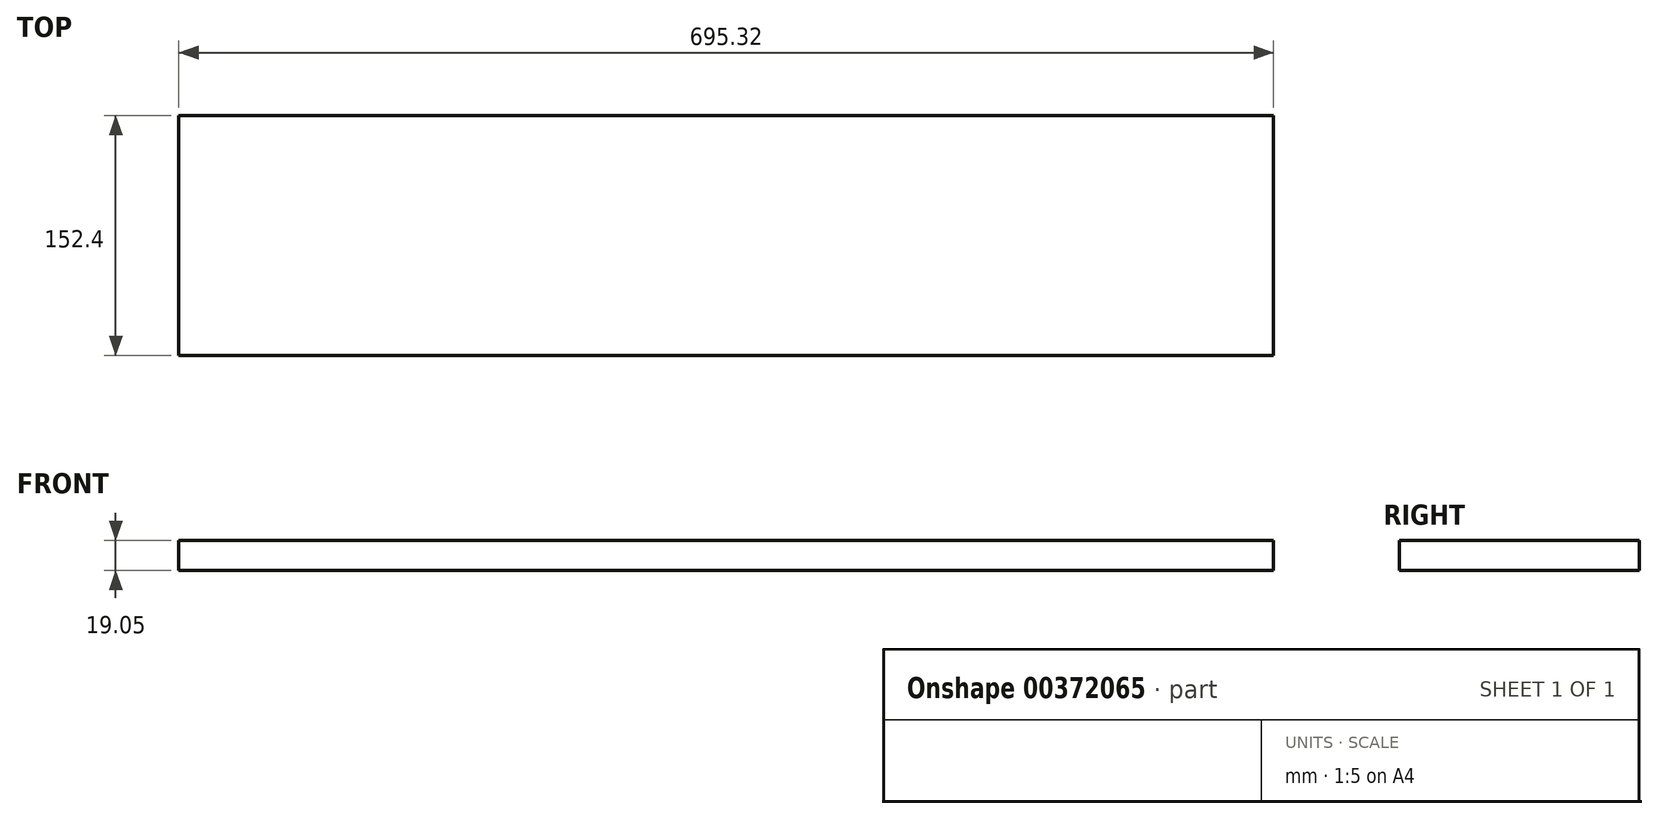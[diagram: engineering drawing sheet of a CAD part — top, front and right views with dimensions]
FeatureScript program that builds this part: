
annotation { "Feature Type Name" : "Feature", "Feature Type Description" : "" }
export const myFeature = defineFeature(function(context is Context, id is Id, definition is map)
    precondition{}
    {
        {
            var Q0;
            Q0=qCreatedBy(makeId("Top.planeOp"),FACE);
            var sketch = newSketch(context, id + "F0", { "sketchPlane" : qUnion([Q0])});
            skLineSegment(sketch, "E0.bottom", {"start": v(0, 0) * mm, "end": v(695.33, 0) * mm});
            skLineSegment(sketch, "E0.top", {"start": v(0, 152.4) * mm, "end": v(695.33, 152.4) * mm});
            skLineSegment(sketch, "E0.left", {"start": v(0, 0) * mm, "end": v(0, 152.4) * mm});
            skLineSegment(sketch, "E0.right", {"start": v(695.33, 0) * mm, "end": v(695.33, 152.4) * mm});
            skSolve(sketch);
        }
        {
            var Q0;
            Q0=makeQuery(id+"F0.imprint","IMPRINT",FACE,{"disambiguationData":[TD([[makeQuery(id+"F0.imprint","IMPRINT",EDGE,{"derivedFrom":sQuery(id+"F0.wireOp",EDGE,"E0.bottom")}),1.0]])]});
            extrude(context, id + "F1", {"entities" : qUnion([Q0]), "oppositeDirection" : true, "depth" : 19.05 * mm});
        }
    });
